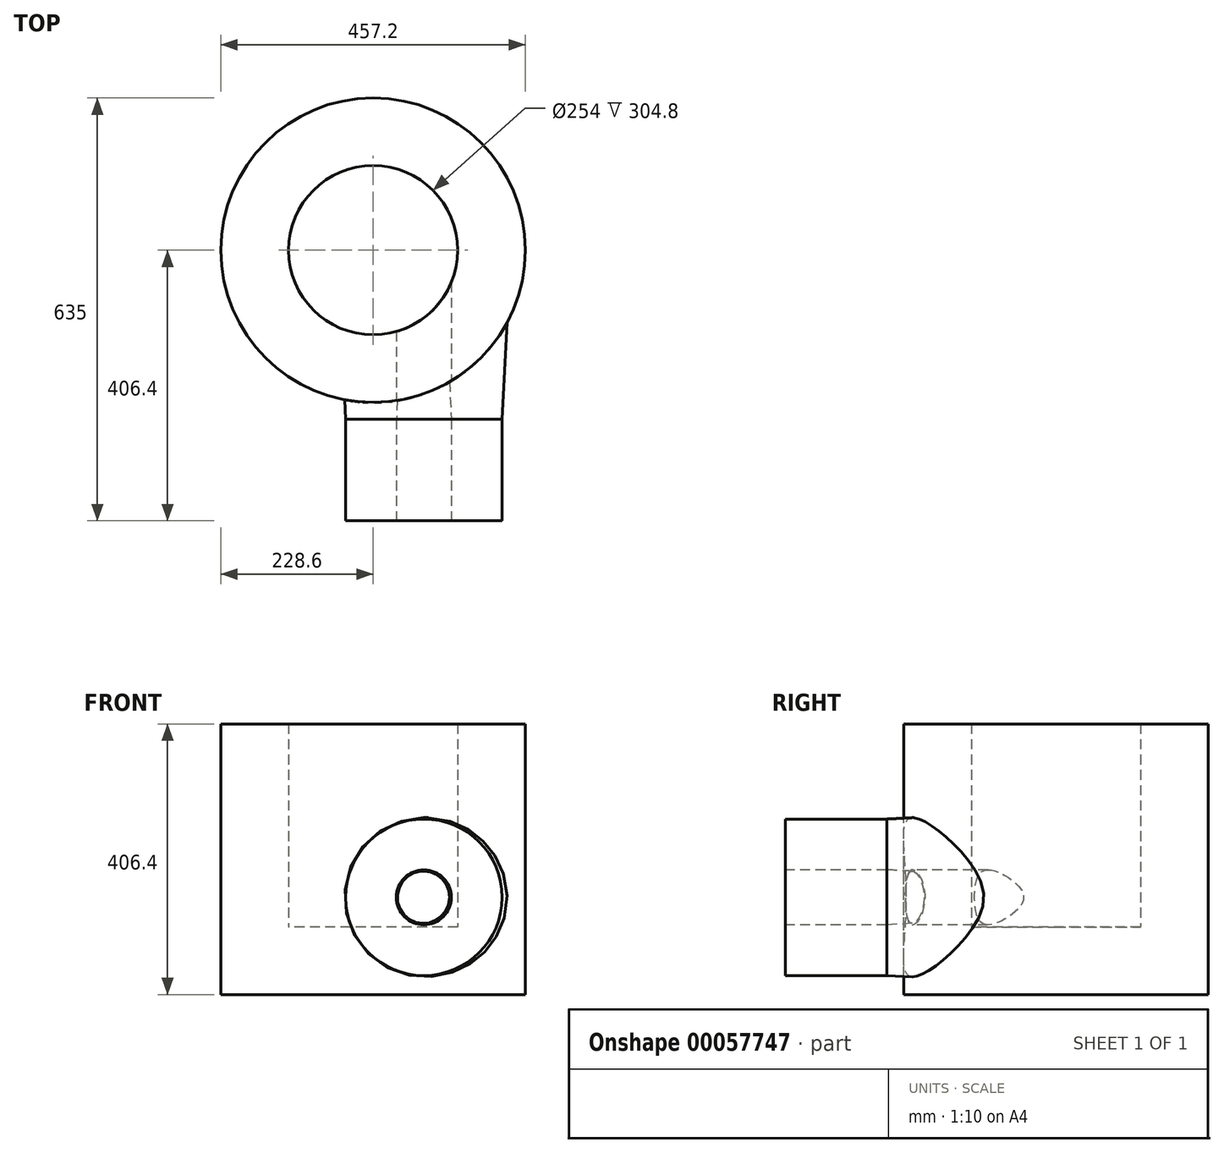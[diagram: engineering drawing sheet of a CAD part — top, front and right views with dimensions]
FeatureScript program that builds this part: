
annotation { "Feature Type Name" : "Feature", "Feature Type Description" : "" }
export const myFeature = defineFeature(function(context is Context, id is Id, definition is map)
    precondition{}
    {
        {
            var Q0;
            Q0=qCreatedBy(makeId("Top.planeOp"),FACE);
            var sketch = newSketch(context, id + "F0", { "sketchPlane" : qUnion([Q0])});
            skCircle(sketch, "E0", {"center": v(0, 0) * mm, "radius": 228.6 * mm});
            skCircle(sketch, "E1", {"center": v(0, 0) * mm, "radius": 127 * mm});
            skSolve(sketch);
        }
        {
            var Q0;
            Q0=makeQuery(id+"F0.imprint","IMPRINT",FACE,{"disambiguationData":[TD([[makeQuery(id+"F0.imprint","IMPRINT",EDGE,{"derivedFrom":sQuery(id+"F0.wireOp",EDGE,"E0")}),1.0]])]});
            var Q1;
            Q1=makeQuery(id+"F0.imprint","IMPRINT",FACE,{"disambiguationData":[TD([[makeQuery(id+"F0.imprint","IMPRINT",EDGE,{"derivedFrom":sQuery(id+"F0.wireOp",EDGE,"E1")}),1.0]])]});
            extrude(context, id + "F3", {"entities" : qUnion([Q0, Q1]), "oppositeDirection" : true, "depth" : 101.6 * mm});
        }
        {
            var Q0;
            Q0=makeQuery(id+"F0.imprint","IMPRINT",FACE,{"disambiguationData":[TD([[makeQuery(id+"F0.imprint","IMPRINT",EDGE,{"derivedFrom":sQuery(id+"F0.wireOp",EDGE,"E0")}),1.0]])]});
            extrude(context, id + "F4", {"entities" : qUnion([Q0]), "operationType" : NewBodyOperationType.ADD, "depth" : 304.8 * mm});
        }
        {
            var Q0;
            Q0=qCreatedBy(makeId("Front.planeOp"),FACE);
            cPlane(context, id + "F5", {"entities" : qUnion([Q0]), "cplaneType" : CPlaneType.OFFSET, "offset" : 254 * mm, "width" : 152.4 * mm, "height" : 152.4 * mm});
        }
        {
            var Q0;
            Q0=qCreatedBy(id+"F5.planeOp",FACE);
            var sketch = newSketch(context, id + "F1", { "sketchPlane" : qUnion([Q0])});
            skPoint(sketch, "E2", {"position": v(76.2, 44.45) * mm});
            skCircle(sketch, "E3", {"center": v(76.2, 44.45) * mm, "radius": 41.28 * mm});
            skCircle(sketch, "E4", {"center": v(76.2, 44.45) * mm, "radius": 117.48 * mm});
            skSolve(sketch);
        }
        {
            var Q0;
            Q0=makeQuery(id+"F1.imprint","IMPRINT",FACE,{"disambiguationData":[TD([[makeQuery(id+"F1.imprint","IMPRINT",EDGE,{"derivedFrom":sQuery(id+"F1.wireOp",EDGE,"E3")}),1.0]])]});
            var Q1;
            Q1=sQuery(id+"F1.wireOp",EDGE,"E3");
            extrude(context, id + "F2", {"entities" : qUnion([Q0]), "operationType" : NewBodyOperationType.REMOVE, "surfaceEntities" : qUnion([Q1]), "oppositeDirection" : true, "depth" : 254 * mm});
        }
        {
            var Q0;
            Q0=makeQuery(id+"F1.imprint","IMPRINT",FACE,{"disambiguationData":[TD([[makeQuery(id+"F1.imprint","IMPRINT",EDGE,{"derivedFrom":sQuery(id+"F1.wireOp",EDGE,"E3")}),-1.0]])]});
            var Q1;
            {var subQ0=sQuery(id+"F0.wireOp",EDGE,"E0");Q1=makeQuery(id+"F4.boolean.opBoolean","MERGE",FACE,{"derivedFrom":[makeQuery(id+"F3.opExtrude","SWEPT_FACE",FACE,{"disambiguationData":[OSD([subQ0])]}),makeQuery(id+"F4.opExtrude","SWEPT_FACE",FACE,{"disambiguationData":[OSD([subQ0])]})]});}
            extrude(context, id + "F6", {"entities" : qUnion([Q0]), "endBound" : BoundingType.UP_TO_SURFACE, "oppositeDirection" : true, "endBoundEntityFace" : qUnion([Q1]), "depth" : 25.4 * mm, "hasDraft" : true, "draftAngle" : 3 * degree, "hasSecondDirection" : true, "secondDirectionOppositeDirection" : false, "secondDirectionDepth" : 152.4 * mm});
        }
    });
